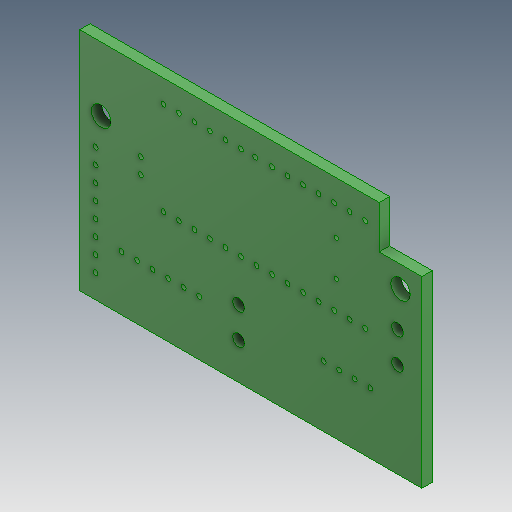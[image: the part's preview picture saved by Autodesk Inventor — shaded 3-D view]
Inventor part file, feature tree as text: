
AUTODESK INVENTOR PART (.ipt)
format: ipt  version: 2020 (Build 240168000, 168)  size: 176,640 bytes
history: native  units: in
note: dims shown in document units (in); Inventor stores cm internally (conversion verified against a paired STEP export)
features: extrude x1, sketch x1, imported_body x1
ambient origin geometry x8: Origin, YZ Plane, XZ Plane, XY Plane, X Axis, Y Axis, Z Axis, Center Point
bodies: Solid1 (feature_tree)
feature tree (3):
  extrude  "Extrusion1"  Depth=1.9291in
  sketch  "Sketch1"  dims[d0=0.126in d1=0.1378in d2=0.1378in d3=1.9291in d4=0.0in d5=0.0in]
  imported_body  "Base1"
